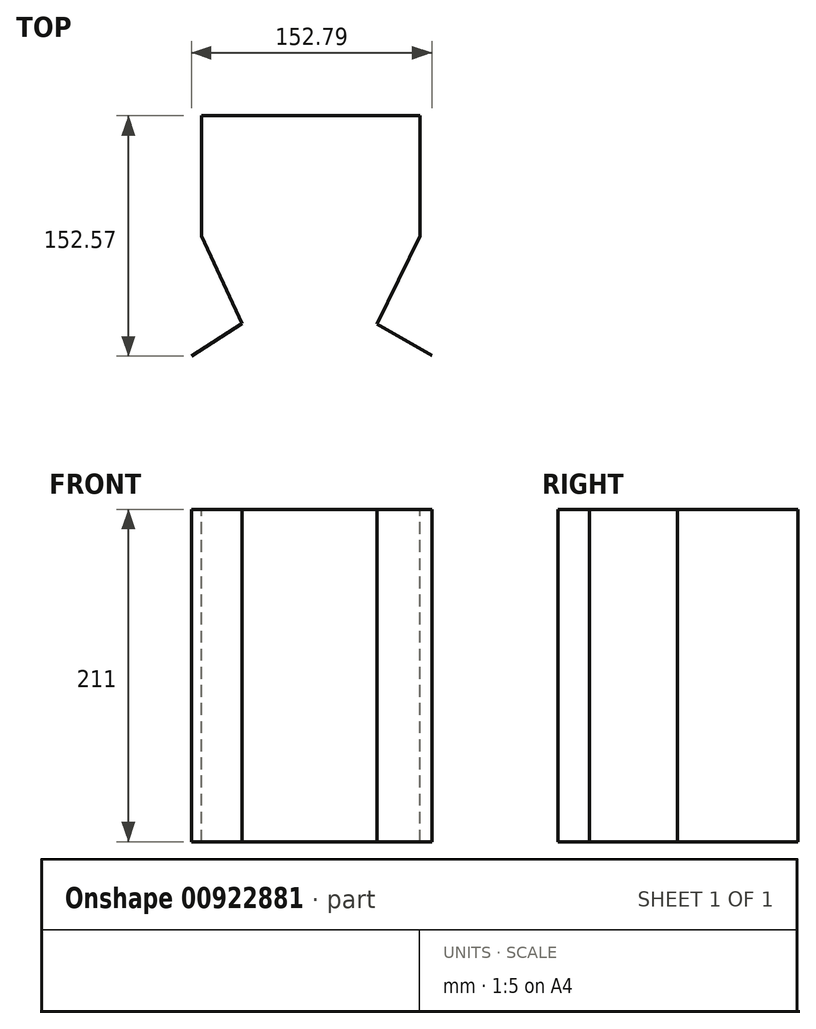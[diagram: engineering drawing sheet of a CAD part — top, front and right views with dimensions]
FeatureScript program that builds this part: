
annotation { "Feature Type Name" : "Feature", "Feature Type Description" : "" }
export const myFeature = defineFeature(function(context is Context, id is Id, definition is map)
    precondition{}
    {
        {
            var Q0;
            Q0=qCreatedBy(makeId("Top.planeOp"),FACE);
            var sketch = newSketch(context, id + "F0", { "sketchPlane" : qUnion([Q0])});
            skLineSegment(sketch, "E0", {"start": v(-76.2, -76.1) * mm, "end": v(-44.02, -55.5) * mm});
            skLineSegment(sketch, "E1", {"start": v(-44.02, -55.5) * mm, "end": v(-69.77, 0) * mm});
            skLineSegment(sketch, "E2", {"start": v(-69.77, 0) * mm, "end": v(-69.77, 76.47) * mm});
            skLineSegment(sketch, "E3", {"start": v(-69.77, 76.47) * mm, "end": v(69.07, 76.47) * mm});
            skLineSegment(sketch, "E4", {"start": v(69.07, 76.47) * mm, "end": v(69.07, 0) * mm});
            skLineSegment(sketch, "E5", {"start": v(69.07, 0) * mm, "end": v(41.6, -55.93) * mm});
            skLineSegment(sketch, "E6", {"start": v(41.6, -55.93) * mm, "end": v(76.58, -75.88) * mm});
            skSolve(sketch);
        }
        {
            var Q0;
            Q0=sQuery(id+"F0.wireOp",EDGE,"E0");
            var Q1;
            Q1=sQuery(id+"F0.wireOp",EDGE,"E1");
            var Q2;
            Q2=sQuery(id+"F0.wireOp",EDGE,"E2");
            var Q3;
            Q3=sQuery(id+"F0.wireOp",EDGE,"E3");
            var Q4;
            Q4=sQuery(id+"F0.wireOp",EDGE,"E4");
            var Q5;
            Q5=sQuery(id+"F0.wireOp",EDGE,"E5");
            var Q6;
            Q6=sQuery(id+"F0.wireOp",EDGE,"E6");
            extrude(context, id + "F1", {"bodyType" : ToolBodyType.SURFACE, "surfaceEntities" : qUnion([Q0, Q1, Q2, Q3, Q4, Q5, Q6]), "depth" : 211 * mm, "offsetDistance" : 25 * mm});
        }
    });
